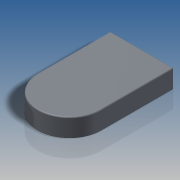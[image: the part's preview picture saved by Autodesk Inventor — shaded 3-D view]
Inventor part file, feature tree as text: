
AUTODESK INVENTOR PART (.ipt)
format: ipt  version: 2016 SP2 (Build 200236200, 236)  size: 119,808 bytes
history: native  units: in
note: dims shown in document units (in); Inventor stores cm internally (conversion verified against a paired STEP export)
features: extrude x1, fillet x1, sketch x1
ambient origin geometry x8: Origin, YZ Plane, XZ Plane, XY Plane, X Axis, Y Axis, Z Axis, Center Point
bodies: Solid1 (feature_tree)
feature tree (3):
  extrude  "Extrusion1"  Depth=0.2205in
  fillet  "Fillet1"  Radius=0.063in
  sketch  "Sketch2"  dims[d0=0.252in d1=0.2205in d2=0.063in d3=0.0in d4=0.0039in]
